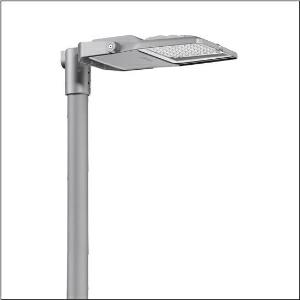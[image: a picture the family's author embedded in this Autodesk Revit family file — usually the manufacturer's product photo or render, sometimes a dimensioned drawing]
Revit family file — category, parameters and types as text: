
# Revit family: floodlight_fl_21_mini___pl52_5xa7776d2d3a_85e1
name_source: partatom
category: Lighting Fixtures
units: mm (PartAtom-declared; Revit-internal decimal feet)

## family parameters
Cut with Voids When Loaded = No
Host = Face
Light Source = No
Part Type = Normal
Room Calculation Point = No
Round Connector Dimension = Use Diameter
Shared = No

## types (1)
- --- (1 x LED, 17840 lm, 142.9 W, 3000K)
    Apparent Load = 143 VA
    CIE Flux Codes = 26 60 98 100 100
    Color Rendering = 70
    Color Temperature = 3000K
    Default Elevation = 1800 mm
    Description = Floodlight FL 21 mini, floodlight, primary light control with lens, of PMMA, primary optical cover: protective disc, of toughened safety glass, transparent, light distribution: PL52, light emission: direct distribution, installation type: surface-mounted, LED, High Power LED, rated luminous flux: 17.840lm, luminous efficacy: 125lm/W, light colour: 730, colour temperature: 3000K, control: flexible luminous flux parameterisation, time-dependent luminous flux control, constant luminous flux control, overheat protection, presetting dimming logarithmic, with terminal, 6-pole, mains connection: 220..240V, AC, 50/60Hz, start of lifetime: 143W, end of service life: 151W, reduction: 63W, luminaire housing, of diecast aluminium, powder-coated, Siteco® metallic grey (DB 702S), corrosivity category C5 mid according to DIN EN ISO 12944, sealing non-destructively replaceable, please order mast flange separately, mast bracket, of steel, galvanised, powder-coated, Siteco® metallic grey (DB 702S), Smart Interface below and above, protection rating (complete): IP66, insulation class (complete): insulation class II (safety insulation), certification: CE, ENEC, VDE, protection symbol: D, impact resistance: IK08, permissible operating ambient temperature: -40..+40°C, permissible operating ambient temperature for outdoor applications: -40..+50°C, standard: DIN EN 12944, LABS conformity tested according to VDMA 24364:2018-05, packaging unit: 1 piece

Light Distribution: PL52
    Height = 70 mm
    Lamp = 1 x LED
    Lamp Light Flux = 17840 lm
    Lamp Power = 142.9 W
    Lamp count = 1
    Length = 485 mm
    Luminous efficacy = 125 lm/W
    Manufacturer = Siteco
    ModVariant = No
    Model = 5XA7776D2D3A
    Number of Poles = 1
    OnlyDefault = Yes
    Power Factor = 1
    Product Name = Floodlight FL 21 mini | PL52
    Product group = floodlight | pylon annexe
    ProductGroupID = 6200
    Protection Class = Protection class II
    Protection Degree = IP 66
    RLX_Detail_Level = 1
    RLX_Emergency_Light_Flux = 0 lm
    RLX_Emergency_Type = 0
    RLX_Emergency_Type_DB = No
    RlxData = <blob elided: 101525 chars, md5=e82be171>
    Socket = socket
    Standby Power = 0 W
    System Light Flux = 17840 lm
    System Power = 143 W
    Type Comments = factory setting: luminous flux: 100 % | dim-lin: 254 | 730 mA
    Type Image = l_1007125.jpg
    URL = http://relux.com
    VarID = @adj_095413
    Voltage = 0 V
    Weight = 0.00 kg
    Width = 337 mm

## geometry (parser evidence)
native form markers: Blend x4, Sweep x11
no freeform markers — native parametric forms only
